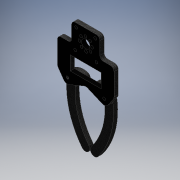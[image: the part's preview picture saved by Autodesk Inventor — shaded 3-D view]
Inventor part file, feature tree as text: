
AUTODESK INVENTOR PART (.ipt)
format: ipt  version: 2016 (Build 200138000, 138)  size: 308,224 bytes
history: native  units: mm
features: fillet x6, extrude x4, sketch x4
ambient origin geometry x8: Origin, YZ Plane, XZ Plane, XY Plane, X Axis, Y Axis, Z Axis, Center Point
bodies: Solid1 (feature_tree)
feature tree (14):
  extrude  "Extrusion1"  Depth=28.0mm
  fillet  "Fillet1"  Radius=80.0mm
  fillet  "Fillet2"  [1 undecoded]
  fillet  "Fillet3"  Radius=38.0mm
  fillet  "Fillet4"  Radius=20.0mm
  fillet  "Fillet5"  Radius=9.599311mm
  extrude  "holes"  Depth=52.184391mm
  extrude  "Extrusion3"  Depth=6.0mm TaperAngle=0.0deg
  extrude  "Extrusion4"  Depth=6.0mm
  fillet  "Fillet6"  Radius=5.0mm
  sketch  "Sketch1"  dims[d0=40.0mm d1=28.0mm d2=80.0mm d3=0.0mm d4=38.0mm d5=20.0mm d6=9.599311mm]
  sketch  "Sketch2"  dims[d7=17.802358mm d8=52.184391mm]
  sketch  "Sketch3"  dims[d9=40.0mm d10=6.0mm d11=0.0mm]
  sketch  "Sketch4"  dims[d12=6.0mm d13=6.0mm d14=5.0mm d15=5.0mm d16=5.0mm d17=12.0mm d18=19.0mm d19=4.0mm d20=80.0mm d22=360.0deg d24=9.0mm d25=20.0mm d26=6.642397mm d27=6.0mm d28=0.0mm d29=4.0mm d35=4.0mm d36=4.0mm d37=4.0mm d40=5.0mm d41=34.0mm d42=5.0mm d43=34.0mm d44=20.0mm d45=44.0mm d46=18.0mm d47=14.0mm d48=4.0mm d49=4.0mm d50=4.0mm d51=10.0mm d52=10.0mm d53=4.0mm d54=6.0mm d55=0.0mm d56=40.0mm d57=5.983671mm d58=105.285438mm d59=8.316395mm d60=14.213796mm d61=28.810962mm d62=11.764364mm d63=48.957431mm d64=60.120145mm d65=6.0mm d66=0.0mm d67=5.968192mm d68=22.471223mm d69=49.787047mm d70=51.189038mm d71=10.0mm d72=13.5mm d73=13.5mm d74=13.5mm d75=13.5mm]
note: 1 required parameter value undecoded (feature->parameter linkage not recoverable at this tier; creation-order binding heuristic only, values carry confidence <= 0.55)
